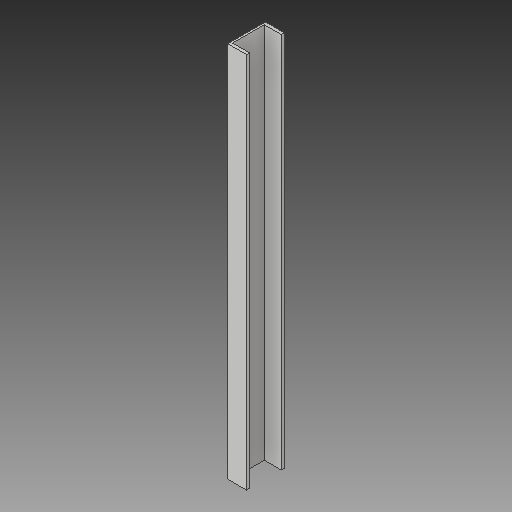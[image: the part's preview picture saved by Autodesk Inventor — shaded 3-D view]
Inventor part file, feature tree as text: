
AUTODESK INVENTOR PART (.ipt)
format: ipt  version: 2019 (Build 230136000, 136)  size: 90,112 bytes
history: native  units: in
note: dims shown in document units (in); Inventor stores cm internally (conversion verified against a paired STEP export)
features: other x3, sketch x1
ambient origin geometry x8: Origin, YZ Plane, XZ Plane, XY Plane, X Axis, Y Axis, Z Axis, Center Point
bodies: Solid1 (feature_tree)
feature tree (4):
  other  "Channel1_MIR_MIR.ipt"
  other  "Solid1::Channel1_MIR_MIR.ipt"
  other  "TaggingFeature1"
  sketch  "Sketch1"  dims[d0=0.3937in]
